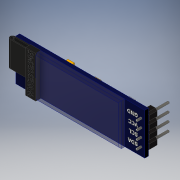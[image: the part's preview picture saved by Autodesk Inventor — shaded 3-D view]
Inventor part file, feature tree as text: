
AUTODESK INVENTOR PART (.ipt)
format: ipt  version: 2019 (Build 230136000, 136)  size: 2,982,400 bytes
history: native  units: mm
features: extrude x20, sketch x20, chamfer x7, projected_geometry x4
ambient origin geometry x8: Origin, YZ Plane, XZ Plane, XY Plane, X Axis, Y Axis, Z Axis, Center Point
bodies: Solid1 (feature_tree), Solid2 (feature_tree), Solid3 (feature_tree), Solid4 (feature_tree), Solid5 (feature_tree), Solid6 (feature_tree), Solid7 (feature_tree), Solid8 (feature_tree), Solid9 (feature_tree), Solid10 (feature_tree), Solid11 (feature_tree), Solid12 (feature_tree), Solid13 (feature_tree), Solid14 (feature_tree), Solid15 (feature_tree), Solid16 (feature_tree), Solid17 (feature_tree)
feature tree (51):
  extrude  "Extrusion1"  Depth=12.1mm
  extrude  "Extrusion2"  Depth=2.3mm TaperAngle=0.0deg
  extrude  "Extrusion3"  Depth=0.15mm TaperAngle=45.0deg
  chamfer  "Chamfer1"  Distance=1.5mm
  extrude  "Extrusion4"  Depth=1.5mm TaperAngle=0.0deg
  extrude  "Extrusion5"  Depth=0.7mm
  chamfer  "Chamfer2"  Distance=0.1mm
  extrude  "Extrusion6"  Depth=7.6mm TaperAngle=0.0deg
  extrude  "Extrusion7"  Depth=0.8mm
  extrude  "Extrusion8"  Depth=0.8mm
  extrude  "Extrusion9"  Depth=0.8mm
  extrude  "Extrusion10"  Depth=0.8mm
  chamfer  "Chamfer3"  Distance=1.0mm
  extrude  "Extrusion11"  Depth=0.02mm TaperAngle=0.0deg
  extrude  "Extrusion12"  Depth=0.02mm TaperAngle=0.0deg
  extrude  "Extrusion13"  Depth=0.1mm TaperAngle=0.0deg
  extrude  "Extrusion14"  Depth=0.1mm TaperAngle=0.0deg
  extrude  "Extrusion15"  Depth=0.1mm TaperAngle=45.0deg
  chamfer  "Chamfer4"  Distance=0.1mm
  extrude  "Extrusion16"  Depth=0.075mm
  extrude  "Extrusion17"  Depth=0.075mm
  chamfer  "Chamfer5"  Distance=0.1mm
  extrude  "Extrusion18"  Depth=0.1mm TaperAngle=45.0deg
  extrude  "Extrusion19"  Depth=0.1mm TaperAngle=0.0deg
  chamfer  "Chamfer6"  Distance=0.1mm
  extrude  "Extrusion20"  Depth=0.1mm TaperAngle=45.0deg
  chamfer  "Chamfer7"  Distance=0.5mm
  sketch  "Sketch1"  dims[d0=37.6mm d1=12.1mm]
  sketch  "Sketch2"  dims[d18=1.1mm d19=0.0mm d36=2.3mm d37=0.0mm]
  sketch  "Sketch3"  dims[d38=1.5mm d39=8.0mm d40=0.0mm d41=0.0mm d42=0.15mm d43=2.0mm d44=45.0deg]
  projected_geometry  "Projected Loop2"
  sketch  "Sketch4"  dims[d45=5.8mm]
  sketch  "Sketch5"  dims[d46=27.5mm]
  sketch  "Sketch6"  dims[d47=3.0mm d48=1.5mm d49=0.0mm]
  sketch  "Sketch7"  dims[d50=3.0mm d51=1.5mm d52=0.0mm]
  sketch  "Sketch8"  dims[d53=0.5mm d54=2.0mm d55=45.0deg d56=0.7mm]
  sketch  "Sketch9"  dims[d57=0.7mm]
  projected_geometry  "Projected Loop3"
  sketch  "Sketch10"  dims[d58=0.7mm]
  sketch  "Sketch11"  dims[d59=0.7mm d60=0.1mm d61=0.0mm]
  sketch  "Sketch12"  dims[d62=0.1mm d63=0.0mm d66=7.6mm d67=0.0mm]
  sketch  "Sketch13"  dims[d68=0.2mm d69=0.0mm d82=0.8mm]
  sketch  "Sketch14"  dims[d83=0.8mm d84=0.8mm]
  projected_geometry  "Projected Loop4"
  projected_geometry  "Projected Loop5"
  sketch  "Sketch15"  dims[d85=0.8mm d86=0.8mm]
  sketch  "Sketch16"  dims[d87=0.8mm d88=0.8mm]
  sketch  "Sketch17"  dims[d89=0.8mm]
  sketch  "Sketch18"  dims[d90=0.8mm d91=1.0mm d92=0.0mm]
  sketch  "Sketch19"  dims[d93=0.09mm d94=2.0mm d95=45.0deg d96=0.02mm d97=0.0mm]
  sketch  "Sketch20"  dims[d102=0.02mm d103=0.0mm d104=0.02mm d105=0.0mm d106=0.1mm d107=0.0mm d108=0.1mm d109=0.0mm d110=0.1mm d111=2.0mm d112=45.0deg d113=0.1mm d114=0.0mm d115=0.075mm d116=0.075mm d117=0.1mm d118=0.0mm d119=0.1mm d120=2.0mm d121=45.0deg d122=0.1mm d123=0.0mm d124=0.1mm d125=0.0mm d126=0.1mm d127=2.0mm d128=45.0deg d129=0.5mm d130=0.5mm d131=0.5mm d132=0.5mm d134=0.25mm d135=0.25mm d136=0.5mm d137=0.0mm d138=0.3mm d139=2.0mm d140=45.0deg]
